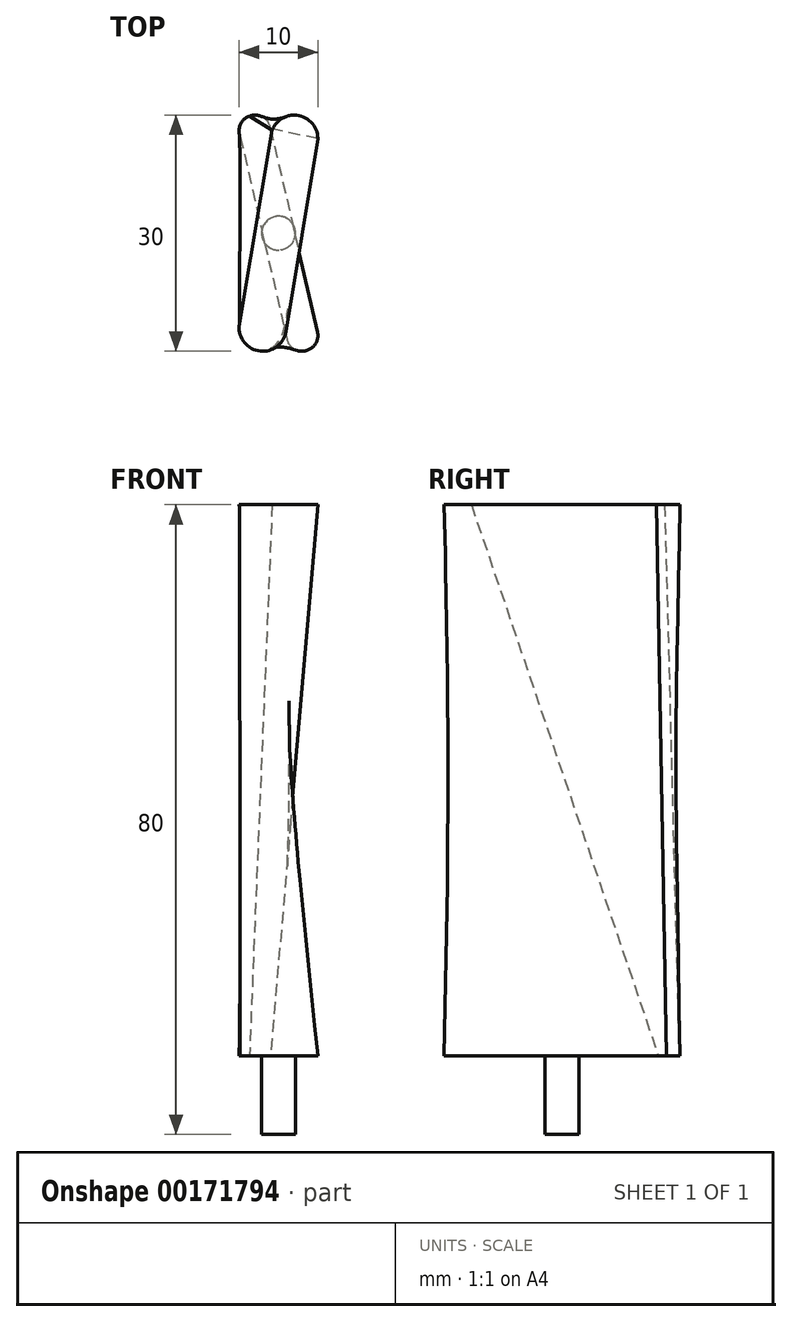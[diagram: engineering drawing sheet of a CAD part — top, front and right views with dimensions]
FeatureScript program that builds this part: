
annotation { "Feature Type Name" : "Feature", "Feature Type Description" : "" }
export const myFeature = defineFeature(function(context is Context, id is Id, definition is map)
    precondition{}
    {
        {
            var Q0;
            Q0=qCreatedBy(makeId("Top.planeOp"),FACE);
            var sketch = newSketch(context, id + "F0", { "sketchPlane" : qUnion([Q0])});
            skCircle(sketch, "E0", {"center": v(0, 0) * mm, "radius": 2.15 * mm});
            skSolve(sketch);
        }
        {
            var Q0;
            Q0=makeQuery(id+"F0.imprint","IMPRINT",FACE,{"disambiguationData":[TD([[makeQuery(id+"F0.imprint","IMPRINT",EDGE,{"derivedFrom":sQuery(id+"F0.wireOp",EDGE,"E0")}),1.0]])]});
            var Q1;
            Q1=sQuery(id+"F0.wireOp",EDGE,"E0");
            extrude(context, id + "F1", {"entities" : qUnion([Q0]), "surfaceEntities" : qUnion([Q1]), "depth" : 10 * mm});
        }
        {
            var Q0;
            Q0=qCreatedBy(makeId("Top.planeOp"),FACE);
            cPlane(context, id + "F2", {"entities" : qUnion([Q0]), "cplaneType" : CPlaneType.OFFSET, "offset" : 10 * mm, "width" : 150 * mm, "height" : 150 * mm});
        }
        {
            var Q0;
            Q0=qCreatedBy(makeId("Top.planeOp"),FACE);
            cPlane(context, id + "F3", {"entities" : qUnion([Q0]), "cplaneType" : CPlaneType.OFFSET, "offset" : 80 * mm, "width" : 150 * mm, "height" : 150 * mm});
        }
        {
            var Q0;
            Q0=qCreatedBy(id+"F3.planeOp",FACE);
            var sketch = newSketch(context, id + "F4", { "sketchPlane" : qUnion([Q0])});
            skPoint(sketch, "E1.middle", {"position": v(0, 0) * mm});
            skArc(sketch, "E2.filletArc", {"start": v(5, 12) * mm, "mid": v(4.12, 14.12) * mm, "end": v(2, 15) * mm});
            skArc(sketch, "E3.filletArc", {"start": v(-5, -12) * mm, "mid": v(-4.12, -14.12) * mm, "end": v(-2, -15) * mm});
            skArc(sketch, "E4", {"start": v(5, 12) * mm, "mid": v(2.54, 14.95) * mm, "end": v(-0.8, 13.06) * mm});
            skPoint(sketch, "E4.second.point", {"position": v(4.12, 14.12) * mm});
            skArc(sketch, "E5", {"start": v(-4.96, -11.5) * mm, "mid": v(-4.99, -11.75) * mm, "end": v(-5, -12) * mm});
            skPoint(sketch, "E5.first.point", {"position": v(-4.54, -13.6) * mm});
            skLineSegment(sketch, "E6", {"start": v(-0.8, 13.06) * mm, "end": v(-4.96, -11.5) * mm});
            skLineSegment(sketch, "E7", {"start": v(5, 12) * mm, "end": v(0.96, -12.49) * mm});
            skArc(sketch, "E8.trimOffspring", {"start": v(-2, -15) * mm, "mid": v(-0.06, -14.29) * mm, "end": v(0.96, -12.49) * mm});
            skSolve(sketch);
        }
        {
            var Q0;
            Q0=qCreatedBy(id+"F2.planeOp",FACE);
            var sketch = newSketch(context, id + "F5", { "sketchPlane" : qUnion([Q0])});
            skArc(sketch, "E9", {"start": v(-1.02, 13.26) * mm, "mid": v(-3.51, 14.93) * mm, "end": v(-4.85, 12.25) * mm});
            skArc(sketch, "E10.MirrorC", {"start": v(4.95, -12.55) * mm, "mid": v(3.45, -14.95) * mm, "end": v(1.05, -13.45) * mm});
            skLineSegment(sketch, "E11", {"start": v(-4.85, 12.25) * mm, "end": v(1.05, -13.45) * mm});
            skLineSegment(sketch, "E12", {"start": v(-1.1, 13.63) * mm, "end": v(4.95, -12.55) * mm});
            skSolve(sketch);
        }
        {
            var Q1;
            Q1 = qSketchRegion(id + "F4", true);
            var Q2;
            Q2 = qSketchRegion(id + "F5", true);
            loft(context, id + "F6", {"operationType" : NewBodyOperationType.ADD, "sheetProfilesArray" : [{ "sheetProfileEntities" : qUnion([Q1]) }, { "sheetProfileEntities" : qUnion([Q2]) }]});
        }
    });
